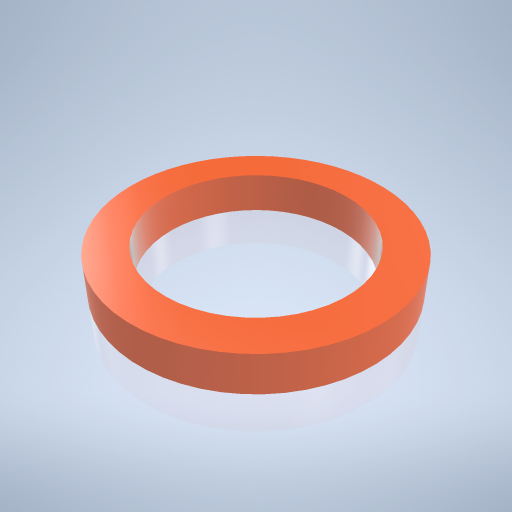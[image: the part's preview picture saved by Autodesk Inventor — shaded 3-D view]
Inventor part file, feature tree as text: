
AUTODESK INVENTOR PART (.ipt)
format: ipt  version: 2024.2 (Build 282272000, 272)  size: 246,272 bytes
history: native  units: mm
features: extrude x1, sketch x1
ambient origin geometry x8: Origin, YZ Plane, XZ Plane, XY Plane, X Axis, Y Axis, Z Axis, Center Point
bodies: Volumenkörper1 (feature_tree)
feature tree (2):
  extrude  "Extrusion1"  Depth=3.5mm
  sketch  "Skizze1"  dims[d0=26.0mm d1=19.0mm d2=3.5mm d3=0.0mm]
